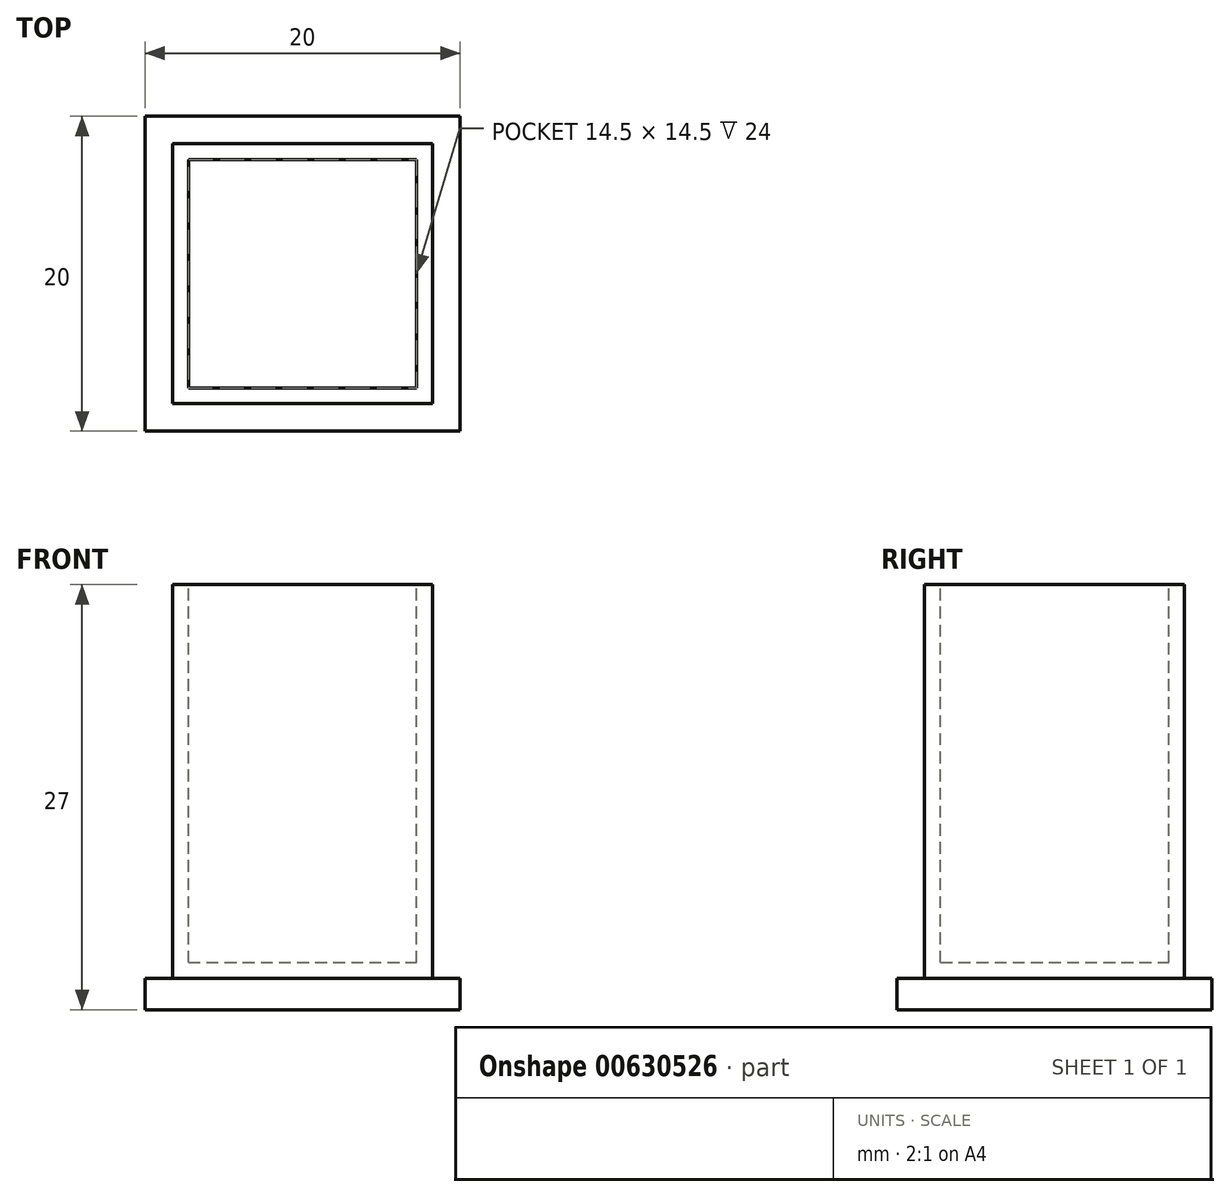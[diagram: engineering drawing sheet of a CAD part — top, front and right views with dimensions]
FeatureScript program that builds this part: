
annotation { "Feature Type Name" : "Feature", "Feature Type Description" : "" }
export const myFeature = defineFeature(function(context is Context, id is Id, definition is map)
    precondition{}
    {
        {
            var Q0;
            Q0=qCreatedBy(makeId("Top.planeOp"),FACE);
            var sketch = newSketch(context, id + "F0", { "sketchPlane" : qUnion([Q0])});
            skLineSegment(sketch, "E0.bottom", {"start": v(-10, 10) * mm, "end": v(10, 10) * mm});
            skLineSegment(sketch, "E0.top", {"start": v(-10, -10) * mm, "end": v(10, -10) * mm});
            skLineSegment(sketch, "E0.left", {"start": v(-10, 10) * mm, "end": v(-10, -10) * mm});
            skLineSegment(sketch, "E0.right", {"start": v(10, 10) * mm, "end": v(10, -10) * mm});
            skLineSegment(sketch, "E1", {"start": v(-10, 10) * mm, "end": v(10, -10) * mm});
            skSolve(sketch);
        }
        {
            var Q0;
            Q0 = qSketchRegion(id + "F0", true);
            extrude(context, id + "F1", {"entities" : qUnion([Q0]), "depth" : 2 * mm, "offsetDistance" : 25 * mm});
        }
        {
            var Q0;
            Q0=makeQuery(id+"F1.opExtrude","CAP_FACE",FACE,{"disambiguationData":[OSD([sQuery(id+"F0.wireOp",EDGE,"E0.bottom"),sQuery(id+"F0.wireOp",EDGE,"E0.top"),sQuery(id+"F0.wireOp",EDGE,"E0.left"),sQuery(id+"F0.wireOp",EDGE,"E0.right")])],"isStart":false});
            var sketch = newSketch(context, id + "F2", { "sketchPlane" : qUnion([Q0])});
            skLineSegment(sketch, "E2.0", {"start": v(-8.25, 8.25) * mm, "end": v(8.25, 8.25) * mm});
            skLineSegment(sketch, "E2.1", {"start": v(-8.25, 8.25) * mm, "end": v(-8.25, -8.25) * mm});
            skLineSegment(sketch, "E2.2", {"start": v(-8.25, -8.25) * mm, "end": v(8.25, -8.25) * mm});
            skLineSegment(sketch, "E2.3", {"start": v(8.25, 8.25) * mm, "end": v(8.25, -8.25) * mm});
            skSolve(sketch);
        }
        {
            var Q0;
            Q0 = qSketchRegion(id + "F2", true);
            extrude(context, id + "F3", {"entities" : qUnion([Q0]), "operationType" : NewBodyOperationType.ADD, "depth" : 25 * mm, "offsetDistance" : 25 * mm});
        }
        {
            var Q0;
            Q0=makeQuery(id+"F3.opExtrude","CAP_FACE",FACE,{"disambiguationData":[OSD([sQuery(id+"F2.wireOp",EDGE,"E2.0"),sQuery(id+"F2.wireOp",EDGE,"E2.1"),sQuery(id+"F2.wireOp",EDGE,"E2.2"),sQuery(id+"F2.wireOp",EDGE,"E2.3")])],"isStart":false});
            var sketch = newSketch(context, id + "F4", { "sketchPlane" : qUnion([Q0])});
            skLineSegment(sketch, "E3.0", {"start": v(7.25, -7.25) * mm, "end": v(7.25, 7.25) * mm});
            skLineSegment(sketch, "E3.1", {"start": v(-7.25, -7.25) * mm, "end": v(7.25, -7.25) * mm});
            skLineSegment(sketch, "E3.2", {"start": v(-7.25, 7.25) * mm, "end": v(-7.25, -7.25) * mm});
            skLineSegment(sketch, "E3.3", {"start": v(7.25, 7.25) * mm, "end": v(-7.25, 7.25) * mm});
            skSolve(sketch);
        }
        {
            var Q0;
            Q0 = qSketchRegion(id + "F4", true);
            extrude(context, id + "F5", {"entities" : qUnion([Q0]), "operationType" : NewBodyOperationType.REMOVE, "oppositeDirection" : true, "depth" : 24 * mm, "offsetDistance" : 25 * mm});
        }
    });
